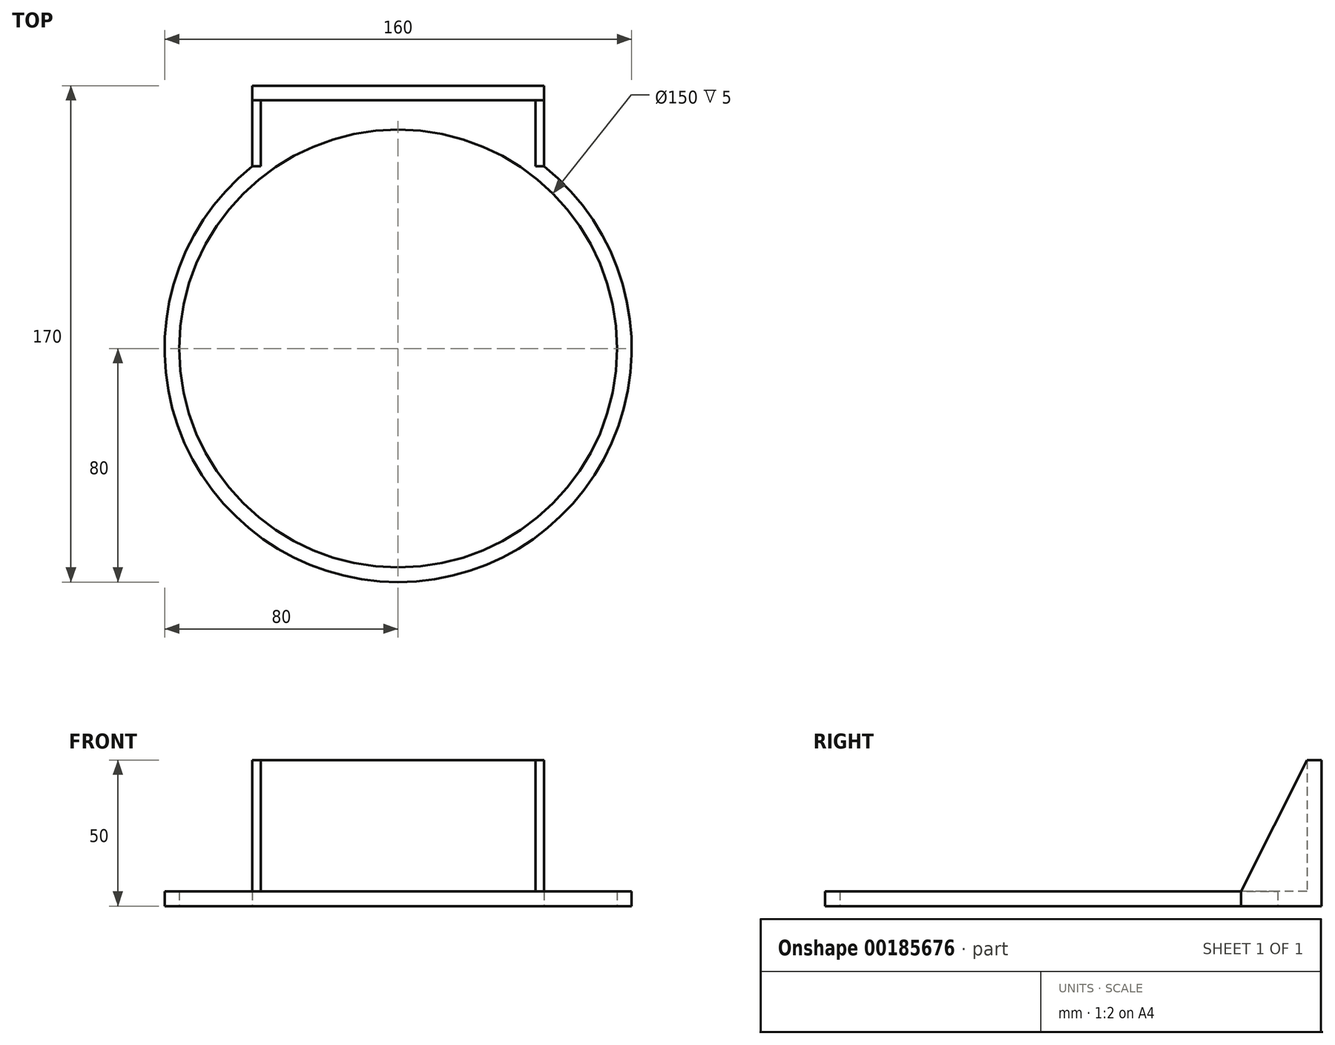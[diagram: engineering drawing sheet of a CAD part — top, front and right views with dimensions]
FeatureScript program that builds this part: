
annotation { "Feature Type Name" : "Feature", "Feature Type Description" : "" }
export const myFeature = defineFeature(function(context is Context, id is Id, definition is map)
    precondition{}
    {
        {
            var Q0;
            Q0=qCreatedBy(makeId("Top.planeOp"),FACE);
            var sketch = newSketch(context, id + "F0", { "sketchPlane" : qUnion([Q0])});
            skCircle(sketch, "E0", {"center": v(0, 0) * mm, "radius": 80 * mm});
            skCircle(sketch, "E1", {"center": v(0, 0) * mm, "radius": 75 * mm});
            skLineSegment(sketch, "E2", {"start": v(-50, 62.45) * mm, "end": v(-50, 90) * mm});
            skLineSegment(sketch, "E3", {"start": v(-50, 90) * mm, "end": v(50, 90) * mm});
            skLineSegment(sketch, "E4", {"start": v(50, 90) * mm, "end": v(50, 62.45) * mm});
            skLineSegment(sketch, "E5", {"start": v(-50, 85) * mm, "end": v(50, 85) * mm});
            skSolve(sketch);
        }
        {
            var Q0;
            Q0=makeQuery(id+"F0.imprint","IMPRINT",FACE,{"disambiguationData":[TD([[makeQuery(id+"F0.imprint","IMPRINT",EDGE,{"derivedFrom":sQuery(id+"F0.wireOp",EDGE,"E1")}),-1.0]])]});
            var Q1;
            {var subQ5=sQuery(id+"F0.wireOp",EDGE,"E5");Q1=makeQuery(id+"F0.imprint","IMPRINT",FACE,{"disambiguationData":[TD([[makeQuery(id+"F0.imprint","IMPRINT",EDGE,{"derivedFrom":subQ5}),-1.0]])]});}
            var Q2;
            {var subQ0=sQuery(id+"F0.wireOp",EDGE,"E3");Q2=makeQuery(id+"F0.imprint","IMPRINT",FACE,{"disambiguationData":[TD([[makeQuery(id+"F0.imprint","IMPRINT",EDGE,{"derivedFrom":subQ0}),-1.0]])]});}
            extrude(context, id + "F1", {"entities" : qUnion([Q0, Q1, Q2]), "depth" : 5 * mm});
        }
        {
            var Q0;
            {var subQ0=sQuery(id+"F0.wireOp",EDGE,"E3");Q0=makeQuery(id+"F0.imprint","IMPRINT",FACE,{"disambiguationData":[TD([[makeQuery(id+"F0.imprint","IMPRINT",EDGE,{"derivedFrom":subQ0}),-1.0]])]});}
            extrude(context, id + "F2", {"entities" : qUnion([Q0]), "operationType" : NewBodyOperationType.ADD, "depth" : 50 * mm});
        }
        {
            var Q0;
            {var subQ0=sQuery(id+"F0.wireOp",EDGE,"E4");Q0=makeQuery(id+"F2.boolean.opBoolean","MERGE",FACE,{"derivedFrom":[makeQuery(id+"F1.opExtrude","SWEPT_FACE",FACE,{"disambiguationData":[OSD([subQ0])]}),makeQuery(id+"F2.opExtrude","SWEPT_FACE",FACE,{"disambiguationData":[OSD([subQ0])]})]});}
            var sketch = newSketch(context, id + "F3", { "sketchPlane" : qUnion([Q0])});
            skLineSegment(sketch, "E6", {"start": v(85, 50) * mm, "end": v(62.45, 5) * mm});
            skLineSegment(sketch, "E7", {"start": v(62.45, 5) * mm, "end": v(85, 5) * mm});
            skLineSegment(sketch, "E8", {"start": v(85, 5) * mm, "end": v(85, 50) * mm});
            skSolve(sketch);
        }
        {
            var Q0;
            Q0=makeQuery(id+"F3.imprint","IMPRINT",FACE,{"disambiguationData":[TD([[makeQuery(id+"F3.imprint","IMPRINT",EDGE,{"derivedFrom":sQuery(id+"F3.wireOp",EDGE,"E6")}),1.0]])]});
            extrude(context, id + "F4", {"entities" : qUnion([Q0]), "oppositeDirection" : true, "depth" : 3 * mm});
        }
        {
            var Q0;
            Q0=makeQuery(id+"F4.opExtrude","SWEPT_BODY",BODY,{"disambiguationData":[OSD([sQuery(id+"F3.wireOp",EDGE,"E6"),sQuery(id+"F3.wireOp",EDGE,"E7"),sQuery(id+"F3.wireOp",EDGE,"E8")])]});
            var Q1;
            Q1=qCreatedBy(makeId("Right.planeOp"),FACE);
            mirror(context, id + "F5", {"operationType" : NewBodyOperationType.ADD, "entities" : qUnion([Q0]), "mirrorPlane" : qUnion([Q1])});
        }
    });
